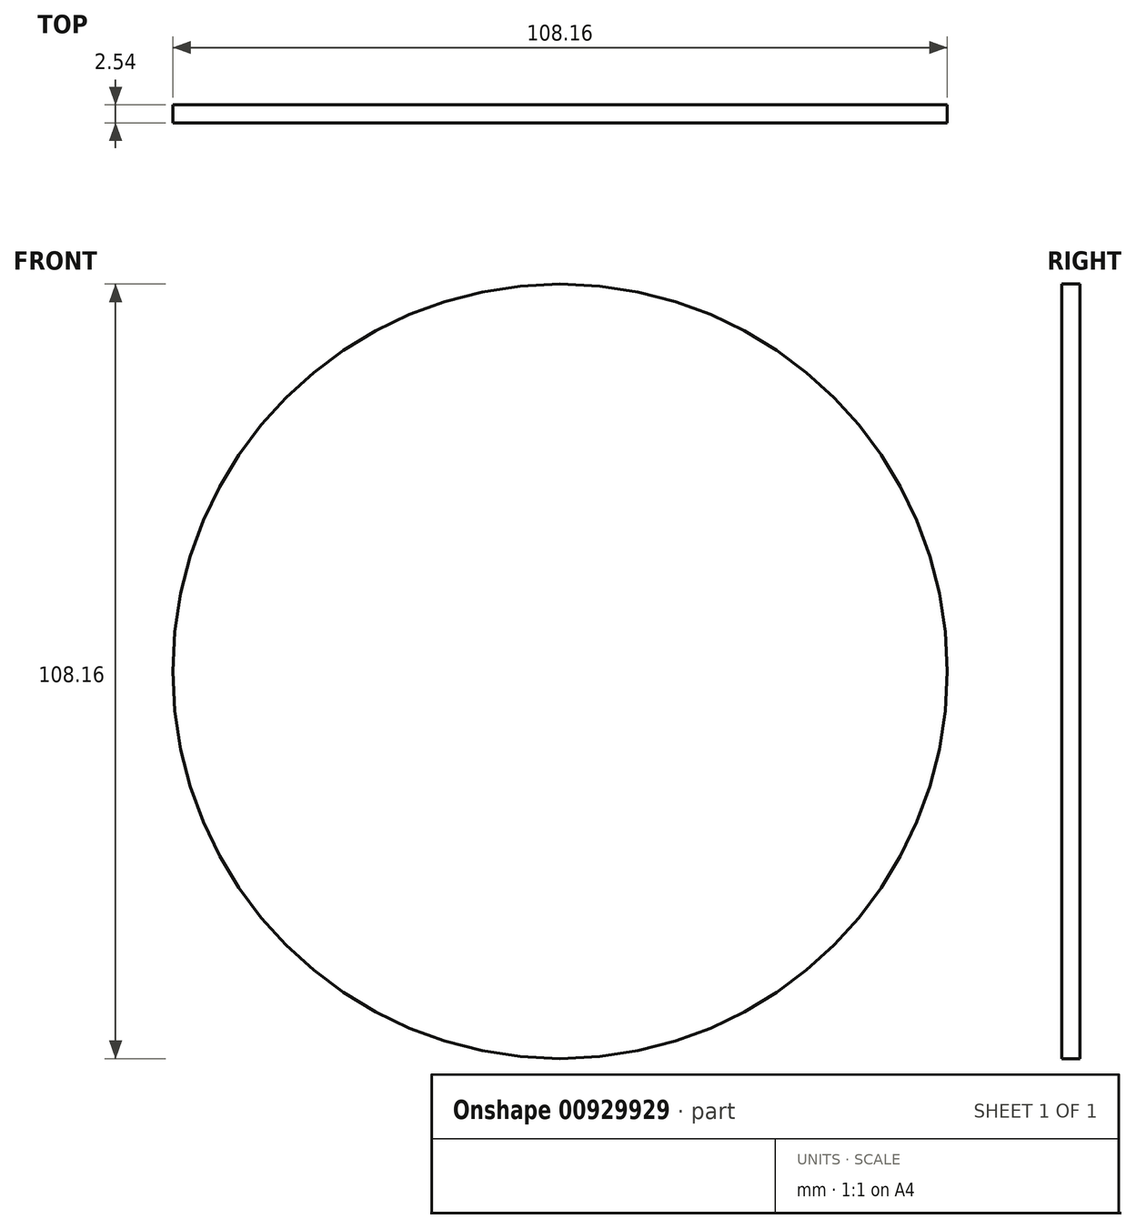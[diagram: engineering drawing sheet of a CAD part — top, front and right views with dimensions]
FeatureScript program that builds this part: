
annotation { "Feature Type Name" : "Feature", "Feature Type Description" : "" }
export const myFeature = defineFeature(function(context is Context, id is Id, definition is map)
    precondition{}
    {
        {
            var Q0;
            Q0=qCreatedBy(makeId("Front.planeOp"),FACE);
            var sketch = newSketch(context, id + "F0", { "sketchPlane" : qUnion([Q0])});
            skCircle(sketch, "E0", {"center": v(0, 0) * mm, "radius": 54.08 * mm});
            skSolve(sketch);
        }
        {
            var Q0;
            Q0=makeQuery(id+"F0.imprint","IMPRINT",FACE,{"disambiguationData":[TD([[makeQuery(id+"F0.imprint","IMPRINT",EDGE,{"derivedFrom":sQuery(id+"F0.wireOp",EDGE,"E0")}),1.0]])]});
            extrude(context, id + "F1", {"entities" : qUnion([Q0]), "depth" : 2.54 * mm, "offsetDistance" : 25.4 * mm});
        }
    });
